# Revit family: Sink-Lavatory-KOHLER-Derring-K-17889
name_source: partatom
category: Plumbing Fixtures
revit_build: Autodesk Revit 2015 (Build: 20140606_1530(x64)
units: mm (PartAtom-declared; Revit-internal decimal feet)

## types (3) — shared parameters
ADA Compliant = Yes
Assembly Code = D2010400
CW Connection = No
Cold Water Inlet = Cold Water Inlet
Date Modified = 11/28/2018
Default Elevation = 36"
Description = 17inch x 14inch under-mount bathroom sink
Drain Included = No
HW Connection = No
Height = 7 3/16"
Hot Water Inlet = Hot Water Inlet
Length = 19 3/8"
Manufacturer = KOHLER Co.
MasterFormat 1995 = 15410
MasterFormat 2004 = 22.41.16
Material = Vitreous China
Product Documentation Link = http://www.us.kohler.com
Product Name = Derring
Product Page URL = http://www.us.kohler.com
URL = https://www.us.kohler.com
Vent Connection = No
Waste Connection = Yes
Waste Water Outlet = Waste Water Outlet
Width = 16 3/8"

## per-type parameters (varying)
| type | Finish | Model | Type |
| K8-Translucent White | Kohler-Vitreous_China-K8-Translucent_White | K-17889-RL-K8 | 1 |
| RB2-Bourbon Rutile | Kohler-Vitreous_China-RB2-Bourbon_Rutile | K-17889-RL-RB2 | 2 |
| RB3-Bluestone Rutile | Kohler-Vitreous_China-RB3-Bluestone_Rutile | K-17889-RL-RB3 | 3 |

## geometry (parser evidence)
native form markers: Sweep x5
no freeform markers — native parametric forms only
